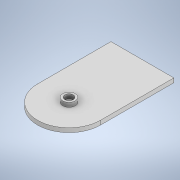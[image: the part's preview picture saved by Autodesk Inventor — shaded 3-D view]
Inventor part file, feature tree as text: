
AUTODESK INVENTOR PART (.ipt)
format: ipt  version: 2020 (Build 240168000, 168)  size: 113,152 bytes
history: native  units: in
note: dims shown in document units (in); Inventor stores cm internally (conversion verified against a paired STEP export)
features: extrude x2, sketch x2, fillet x1
ambient origin geometry x8: Origin, YZ Plane, XZ Plane, XY Plane, X Axis, Y Axis, Z Axis, Center Point
bodies: Solid1 (feature_tree)
feature tree (5):
  extrude  "Extrusion1"  Depth=5.0in
  fillet  "Fillet1"  Radius=0.2in
  extrude  "Extrusion2"  Depth=0.2in
  sketch  "Sketch1"  dims[d0=3.0in d1=5.0in d2=0.2in d3=0.0in]
  sketch  "Sketch2"  dims[d4=1.5in d5=0.6in d6=0.4in d7=0.2in d8=0.0in]
